# Revit family: AirPro_Island Mount
name_source: partatom
category: Generic Models
revit_build: Autodesk Revit Architecture 2013 (Build: 20120221_2030(x64)
units: mm (PartAtom-declared; Revit-internal decimal feet)

## types (4) — shared parameters
Cage Array st = 3 "
Depth = 28.5 "
Description = Air Pro Locker Wall Mount(Starter)
Keynote = Wenger Air Pro Locker(Starter)
Manufacturer = Wenger Corporation
URL = http://www.wengercorp.com

## per-type parameters (varying)
| type | Cage Array | Hang Hook Width | School Color | Seat Width | Seat and Shelf Laminate | Width | Width Bar |
| 15" | 4 | 14.75 " | Poche | 14.75 " | Poche | 16.25 " | 15 " |
| 18" | 5 | 17.75 " | <By Category> | 17.75 " | <By Category> | 19.25 " | 18 " |
| 24" | 7 | 23.75 " | <By Category> | 23.75 " | <By Category> | 25.25 " | 24 " |
| 30" | 9 | 29.75 " | <By Category> | 29.75 " | <By Category> | 31.25 " | 30 " |

note: column(s) folded — value = type name in every type: Model

## geometry (parser evidence)
native form markers: Sweep x16
no freeform markers — native parametric forms only
